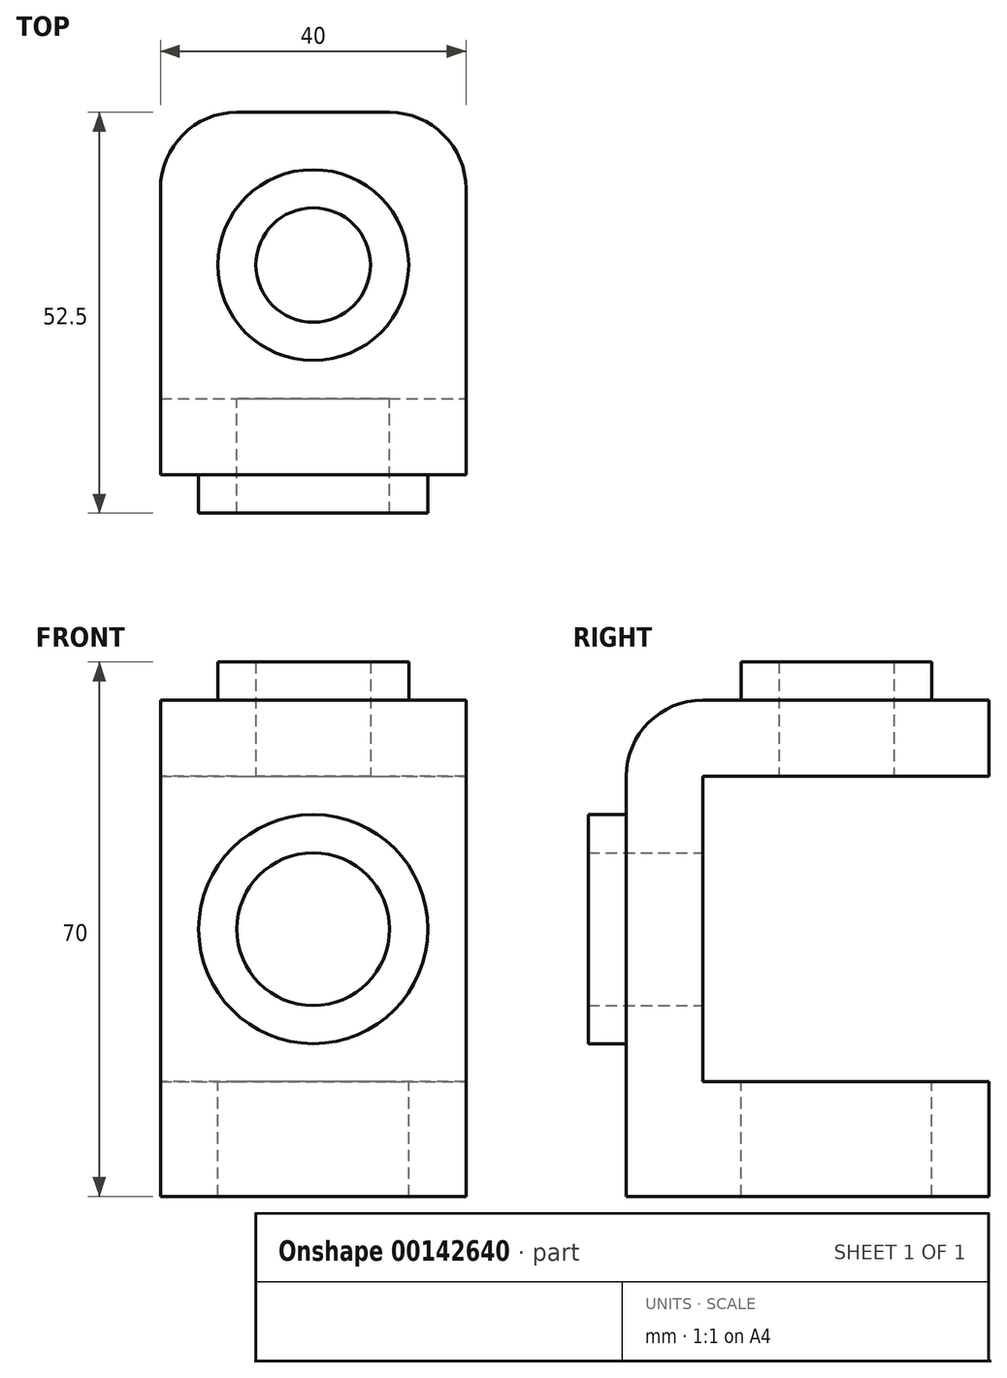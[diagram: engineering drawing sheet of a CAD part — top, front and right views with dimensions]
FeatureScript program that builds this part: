
annotation { "Feature Type Name" : "Feature", "Feature Type Description" : "" }
export const myFeature = defineFeature(function(context is Context, id is Id, definition is map)
    precondition{}
    {
        {
            var Q0;
            Q0=qCreatedBy(makeId("Front.planeOp"),FACE);
            var sketch = newSketch(context, id + "F9", { "sketchPlane" : qUnion([Q0])});
            skLineSegment(sketch, "E0", {"start": v(0, 59.08) * mm, "end": v(0, -62.4) * mm, "construction": true});
            skLineSegment(sketch, "E1", {"start": v(-55.55, 0) * mm, "end": v(55.07, 0) * mm, "construction": true});
            skLineSegment(sketch, "E2", {"start": v(-20, 30) * mm, "end": v(20, 30) * mm});
            skLineSegment(sketch, "E3", {"start": v(20, 30) * mm, "end": v(20, -30) * mm});
            skLineSegment(sketch, "E4", {"start": v(20, -30) * mm, "end": v(-20, -30) * mm});
            skLineSegment(sketch, "E5", {"start": v(-20, -30) * mm, "end": v(-20, 30) * mm});
            skSolve(sketch);
        }
        {
            var Q0;
            Q0 = qSketchRegion(id + "F9", true);
            extrude(context, id + "F0", {"entities" : qUnion([Q0]), "depth" : 47.5 * mm});
        }
        {
            var Q0;
            Q0=qCreatedBy(makeId("Front.planeOp"),FACE);
            var sketch = newSketch(context, id + "F10", { "sketchPlane" : qUnion([Q0])});
            skLineSegment(sketch, "E6", {"start": v(-41.1, 20) * mm, "end": v(40.01, 20) * mm});
            skLineSegment(sketch, "E7", {"start": v(40.01, 20) * mm, "end": v(40.01, -20) * mm});
            skLineSegment(sketch, "E8", {"start": v(40.01, -20) * mm, "end": v(-41.1, -20) * mm});
            skLineSegment(sketch, "E9", {"start": v(-41.1, -20) * mm, "end": v(-41.1, 20) * mm});
            skSolve(sketch);
        }
        {
            var Q0;
            Q0=makeQuery(id+"F10.imprint","IMPRINT",FACE,{"disambiguationData":[TD([[makeQuery(id+"F10.imprint","IMPRINT",EDGE,{"derivedFrom":sQuery(id+"F10.wireOp",EDGE,"E6")}),-1.0]])]});
            extrude(context, id + "F1", {"entities" : qUnion([Q0]), "operationType" : NewBodyOperationType.REMOVE, "depth" : 37.5 * mm});
        }
        {
            var Q0;
            Q0=makeQuery(id+"F0.opExtrude","SWEPT_FACE",FACE,{"disambiguationData":[OSD([sQuery(id+"F9.wireOp",EDGE,"E2")])]});
            var sketch = newSketch(context, id + "F2", { "sketchPlane" : qUnion([Q0])});
            skCircle(sketch, "E10", {"center": v(0, -20) * mm, "radius": 12.5 * mm});
            skCircle(sketch, "E11", {"center": v(0, -20) * mm, "radius": 7.5 * mm});
            skLineSegment(sketch, "E12.0.0", {"start": v(-20, 0) * mm, "end": v(20, 0) * mm});
            skLineSegment(sketch, "E12.0.1", {"start": v(20, 0) * mm, "end": v(20, -47.5) * mm});
            skLineSegment(sketch, "E12.0.2", {"start": v(20, -47.5) * mm, "end": v(-20, -47.5) * mm});
            skLineSegment(sketch, "E12.0.3", {"start": v(-20, -47.5) * mm, "end": v(-20, 0) * mm});
            skSolve(sketch);
        }
        {
            var Q0;
            Q0=makeQuery(id+"F0.opExtrude","SWEPT_FACE",FACE,{"disambiguationData":[OSD([sQuery(id+"F9.wireOp",EDGE,"E4")])]});
            var sketch = newSketch(context, id + "F3", { "sketchPlane" : qUnion([Q0])});
            skCircle(sketch, "E13.0", {"center": v(0, 20) * mm, "radius": 12.5 * mm});
            skCircle(sketch, "E14.0", {"center": v(0, 20) * mm, "radius": 7.5 * mm});
            skSolve(sketch);
        }
        {
            var Q0;
            Q0=makeQuery(id+"F3.imprint","IMPRINT",FACE,{"disambiguationData":[TD([[makeQuery(id+"F3.imprint","IMPRINT",EDGE,{"derivedFrom":sQuery(id+"F3.wireOp",EDGE,"E13.0")}),-1.0]])]});
            var Q1;
            Q1=sQuery(id+"F3.wireOp",EDGE,"E13.0");
            extrude(context, id + "F4", {"entities" : qUnion([Q0]), "operationType" : NewBodyOperationType.ADD, "surfaceEntities" : qUnion([Q1]), "depth" : 5 * mm});
        }
        {
            var Q0;
            Q0=makeQuery(id+"F2.imprint","IMPRINT",FACE,{"disambiguationData":[TD([[makeQuery(id+"F2.imprint","IMPRINT",EDGE,{"derivedFrom":sQuery(id+"F2.wireOp",EDGE,"E10")}),1.0]])]});
            extrude(context, id + "F11", {"entities" : qUnion([Q0]), "operationType" : NewBodyOperationType.ADD, "depth" : 5 * mm});
        }
        {
            var Q0;
            Q0=makeQuery(id+"F0.opExtrude","CAP_EDGE",EDGE,{"disambiguationData":[OSD([sQuery(id+"F9.wireOp",EDGE,"E4")])],"isStart":false});
            var Q1;
            Q1=makeQuery(id+"F0.opExtrude","CAP_EDGE",EDGE,{"disambiguationData":[OSD([sQuery(id+"F9.wireOp",EDGE,"E2")])],"isStart":false});
            var Q2;
            {var subQ0=sQuery(id+"F9.wireOp",EDGE,"E4");var subQ1=sQuery(id+"F9.wireOp",EDGE,"E3");Q2=makeQuery(id+"F1.boolean.opBoolean","SPLIT",EDGE,{"disambiguationData":[TD([makeQuery(id+"F0.opExtrude","SWEPT_FACE",FACE,{"disambiguationData":[OSD([subQ0])]})])],"derivedFrom":makeQuery(id+"F0.opExtrude","CAP_EDGE",EDGE,{"disambiguationData":[OSD([subQ1])],"isStart":true})});}
            var Q3;
            {var subQ0=sQuery(id+"F9.wireOp",EDGE,"E5");var subQ1=sQuery(id+"F9.wireOp",EDGE,"E4");Q3=makeQuery(id+"F1.boolean.opBoolean","SPLIT",EDGE,{"disambiguationData":[TD([makeQuery(id+"F0.opExtrude","SWEPT_FACE",FACE,{"disambiguationData":[OSD([subQ1])]})])],"derivedFrom":makeQuery(id+"F0.opExtrude","CAP_EDGE",EDGE,{"disambiguationData":[OSD([subQ0])],"isStart":true})});}
            var Q4;
            {var subQ0=sQuery(id+"F9.wireOp",EDGE,"E2");var subQ1=sQuery(id+"F9.wireOp",EDGE,"E5");Q4=makeQuery(id+"F1.boolean.opBoolean","SPLIT",EDGE,{"disambiguationData":[TD([makeQuery(id+"F0.opExtrude","SWEPT_FACE",FACE,{"disambiguationData":[OSD([subQ0])]})])],"derivedFrom":makeQuery(id+"F0.opExtrude","CAP_EDGE",EDGE,{"disambiguationData":[OSD([subQ1])],"isStart":true})});}
            var Q5;
            {var subQ0=sQuery(id+"F9.wireOp",EDGE,"E2");var subQ1=sQuery(id+"F9.wireOp",EDGE,"E3");Q5=makeQuery(id+"F1.boolean.opBoolean","SPLIT",EDGE,{"disambiguationData":[TD([makeQuery(id+"F0.opExtrude","SWEPT_FACE",FACE,{"disambiguationData":[OSD([subQ0])]})])],"derivedFrom":makeQuery(id+"F0.opExtrude","CAP_EDGE",EDGE,{"disambiguationData":[OSD([subQ1])],"isStart":true})});}
            fillet(context, id + "F5", {"entities" : qUnion([Q0, Q1, Q2, Q3, Q4, Q5]), "radius" : 10 * mm, "tangentPropagation" : true, "allowEdgeOverflow" : false});
        }
        {
            var Q0;
            Q0=makeQuery(id+"F0.opExtrude","CAP_FACE",FACE,{"disambiguationData":[OSD([sQuery(id+"F9.wireOp",EDGE,"E2"),sQuery(id+"F9.wireOp",EDGE,"E3"),sQuery(id+"F9.wireOp",EDGE,"E4"),sQuery(id+"F9.wireOp",EDGE,"E5")])],"isStart":false});
            var sketch = newSketch(context, id + "F12", { "sketchPlane" : qUnion([Q0])});
            skCircle(sketch, "E15", {"center": v(0, 0) * mm, "radius": 15 * mm});
            skCircle(sketch, "E16", {"center": v(0, 0) * mm, "radius": 10 * mm});
            skSolve(sketch);
        }
        {
            var Q0;
            Q0=makeQuery(id+"F12.imprint","IMPRINT",FACE,{"disambiguationData":[TD([[makeQuery(id+"F12.imprint","IMPRINT",EDGE,{"derivedFrom":sQuery(id+"F12.wireOp",EDGE,"E15")}),1.0]])]});
            extrude(context, id + "F13", {"entities" : qUnion([Q0]), "operationType" : NewBodyOperationType.ADD, "depth" : 5 * mm});
        }
        {
            var Q0;
            Q0=makeQuery(id+"F2.imprint","IMPRINT",FACE,{"disambiguationData":[TD([[makeQuery(id+"F2.imprint","IMPRINT",EDGE,{"derivedFrom":sQuery(id+"F2.wireOp",EDGE,"E11")}),1.0]])]});
            extrude(context, id + "F6", {"entities" : qUnion([Q0]), "operationType" : NewBodyOperationType.REMOVE, "oppositeDirection" : true, "depth" : 25 * mm});
        }
        {
            var Q0;
            Q0=makeQuery(id+"F4.boolean.opBoolean","SPLIT",FACE,{"disambiguationData":[TD([makeQuery(id+"F4.opExtrude","SWEPT_FACE",FACE,{"disambiguationData":[OSD([sQuery(id+"F3.wireOp",EDGE,"E14.0")])]})])],"derivedFrom":makeQuery(id+"F0.opExtrude","SWEPT_FACE",FACE,{"disambiguationData":[OSD([sQuery(id+"F9.wireOp",EDGE,"E4")])]})});
            extrude(context, id + "F7", {"entities" : qUnion([Q0]), "operationType" : NewBodyOperationType.REMOVE, "oppositeDirection" : true, "depth" : 25 * mm});
        }
        {
            var Q0;
            Q0=makeQuery(id+"F13.boolean.opBoolean","SPLIT",FACE,{"disambiguationData":[TD([makeQuery(id+"F13.opExtrude","SWEPT_FACE",FACE,{"disambiguationData":[OSD([sQuery(id+"F12.wireOp",EDGE,"E16")])]})])],"derivedFrom":makeQuery(id+"F0.opExtrude","CAP_FACE",FACE,{"disambiguationData":[OSD([sQuery(id+"F9.wireOp",EDGE,"E2"),sQuery(id+"F9.wireOp",EDGE,"E3"),sQuery(id+"F9.wireOp",EDGE,"E4"),sQuery(id+"F9.wireOp",EDGE,"E5")])],"isStart":false})});
            extrude(context, id + "F8", {"entities" : qUnion([Q0]), "operationType" : NewBodyOperationType.REMOVE, "oppositeDirection" : true, "depth" : 25 * mm});
        }
    });
